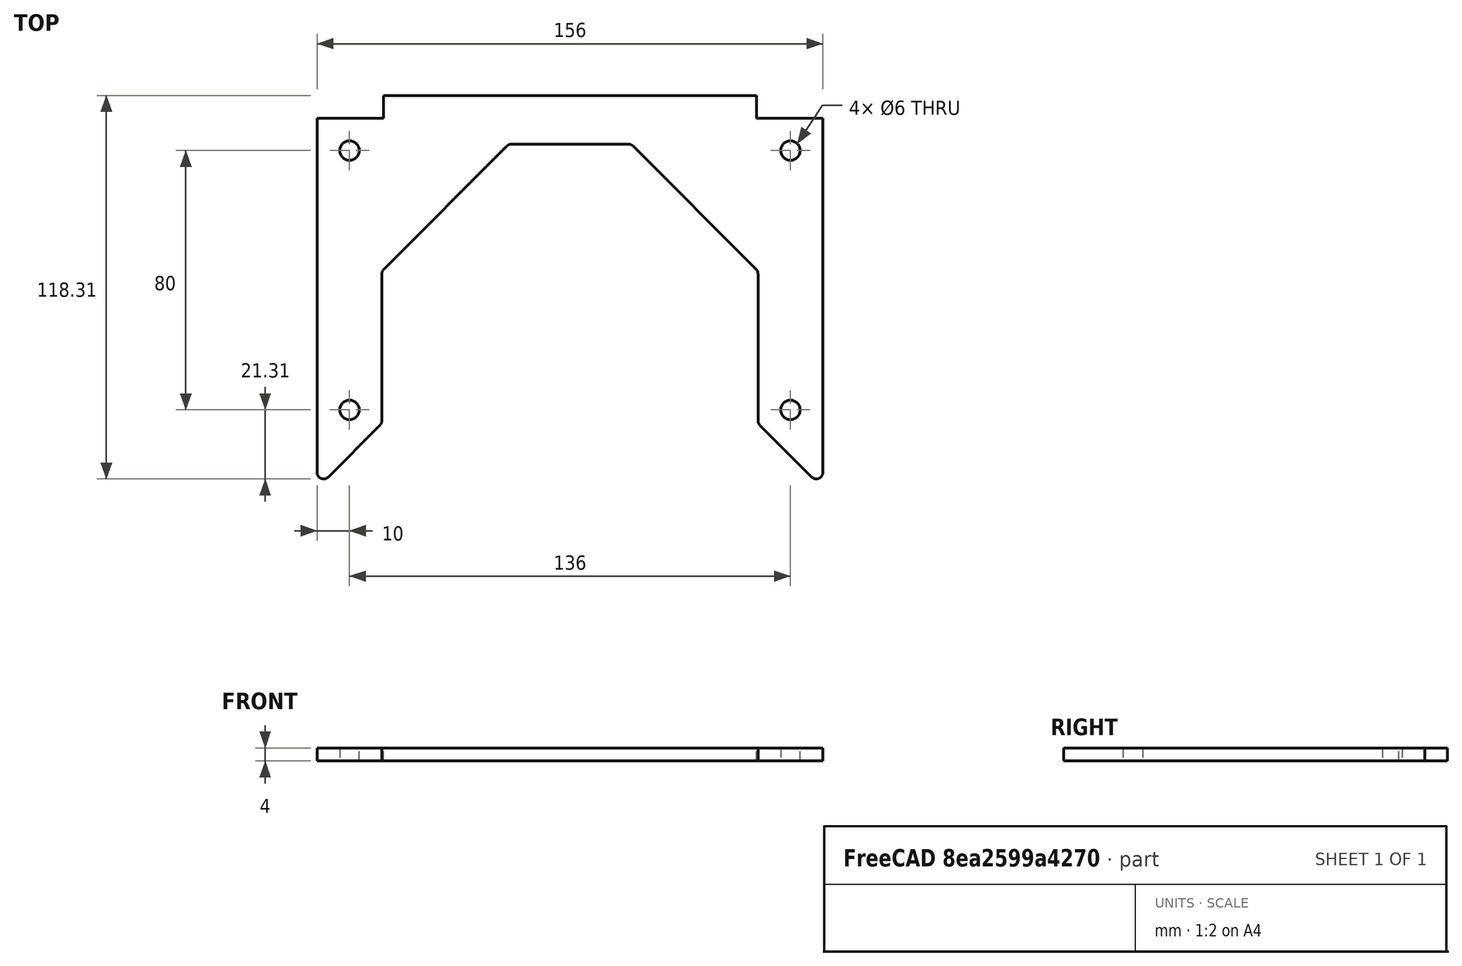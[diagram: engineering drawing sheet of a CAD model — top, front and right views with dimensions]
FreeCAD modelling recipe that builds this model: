
FCSTD DOCUMENT  (FreeCAD 0.19R24267 +99 (Git))
Label: V2 Enclosure middle U bracket slotted panel without cable notch
License: All rights reserved
LicenseURL: http://en.wikipedia.org/wiki/All_rights_reserved
objects: Sketcher::SketchObject×1, PartDesign::Pad×1, PartDesign::Body×1
note: 4 computed .brp shape members not serialized (recipe doc carries the construction recipe); baked Part::Feature solids carry a one-line shape summary decoded from their .brp

FEATURE [Sketcher::SketchObject] Sketch
  FullyConstrained = true
  MapMode = 5
  Support = -> [XY_Plane]
  sketch-geometry (35):
    g0: LineSegment StartX=-68 StartY=0 StartZ=0 EndX=-68 EndY=-114.142 EndZ=0
    g1: Circle CenterX=-68 CenterY=-100 CenterZ=0 NormalX=0 NormalY=0 NormalZ=1 AngleXU=0 Radius=3
    g2: LineSegment StartX=68 StartY=0 StartZ=0 EndX=68 EndY=-114.142 EndZ=0
    g3: Circle CenterX=68 CenterY=-100 CenterZ=0 NormalX=0 NormalY=0 NormalZ=1 AngleXU=0 Radius=3
    g4: LineSegment StartX=-78 StartY=-10 StartZ=0 EndX=-78 EndY=-119.314 EndZ=0
    g5: LineSegment StartX=-58 StartY=-58 StartZ=0 EndX=-58 EndY=-103.314 EndZ=0
    g6: LineSegment StartX=-57.4142 StartY=-56.5858 StartZ=0 EndX=-19.4142 EndY=-18.5858 EndZ=0
    g7: LineSegment StartX=19.4142 StartY=-18.5858 StartZ=0 EndX=57.4142 EndY=-56.5858 EndZ=0
    g8: LineSegment StartX=58 StartY=-58 StartZ=0 EndX=58 EndY=-103.314 EndZ=0
    g9: LineSegment StartX=58.5858 StartY=-104.728 StartZ=0 EndX=74.5858 EndY=-120.728 EndZ=0
    g10: LineSegment StartX=78 StartY=-119.314 StartZ=0 EndX=78 EndY=-10 EndZ=0
    g11: LineSegment StartX=57.5 StartY=10 StartZ=0 EndX=-57.5 EndY=10 EndZ=0
    g12: LineSegment StartX=-74.5858 StartY=-120.728 StartZ=0 EndX=-58.5858 EndY=-104.728 EndZ=0
    g13: ArcOfCircle CenterX=-76 CenterY=-119.314 CenterZ=0 NormalX=0 NormalY=0 NormalZ=1 AngleXU=0 Radius=2 StartAngle=3.14159 EndAngle=5.49779
    g14: ArcOfCircle CenterX=-60 CenterY=-103.314 CenterZ=0 NormalX=0 NormalY=0 NormalZ=1 AngleXU=0 Radius=2 StartAngle=5.49779 EndAngle=6.28319
    g15: ArcOfCircle CenterX=60 CenterY=-103.314 CenterZ=0 NormalX=0 NormalY=0 NormalZ=1 AngleXU=0 Radius=2 StartAngle=3.14159 EndAngle=3.92699
    g16: ArcOfCircle CenterX=76 CenterY=-119.314 CenterZ=0 NormalX=0 NormalY=0 NormalZ=1 AngleXU=0 Radius=2 StartAngle=3.92699 EndAngle=6.28319
    g17: ArcOfCircle CenterX=-56 CenterY=-58 CenterZ=0 NormalX=0 NormalY=0 NormalZ=1 AngleXU=0 Radius=2 StartAngle=2.35619 EndAngle=3.14159
    g18: ArcOfCircle CenterX=-18 CenterY=-20 CenterZ=0 NormalX=0 NormalY=0 NormalZ=1 AngleXU=0 Radius=2 StartAngle=1.5708 EndAngle=2.35619
    g19: ArcOfCircle CenterX=18 CenterY=-20 CenterZ=0 NormalX=0 NormalY=0 NormalZ=1 AngleXU=0 Radius=2 StartAngle=0.785398 EndAngle=1.5708
    g20: ArcOfCircle CenterX=56 CenterY=-58 CenterZ=0 NormalX=0 NormalY=0 NormalZ=1 AngleXU=0 Radius=2 StartAngle=0 EndAngle=0.785398
    g21: Circle CenterX=-68 CenterY=-100 CenterZ=0 NormalX=0 NormalY=0 NormalZ=1 AngleXU=0 Radius=10
    g22: Circle CenterX=68 CenterY=-100 CenterZ=0 NormalX=0 NormalY=0 NormalZ=1 AngleXU=0 Radius=10
    g23: GeomPoint X=0 Y=-10 Z=0
    g24: GeomPoint X=0 Y=10 Z=0
    g25: LineSegment StartX=-78 StartY=-10 StartZ=0 EndX=-57.5 EndY=-10 EndZ=0
    g26: LineSegment StartX=57.5 StartY=-10 StartZ=0 EndX=78 EndY=-10 EndZ=0
    g27: LineSegment StartX=-57.5 StartY=-10 StartZ=0 EndX=-57.5 EndY=-3 EndZ=0
    g28: LineSegment StartX=-57.5 StartY=-3 StartZ=0 EndX=-57.5 EndY=10 EndZ=0
    g29: LineSegment StartX=57.5 StartY=10 StartZ=0 EndX=57.5 EndY=-3 EndZ=0
    g30: LineSegment StartX=57.5 StartY=-3 StartZ=0 EndX=57.5 EndY=-10 EndZ=0
    g31: LineSegment StartX=57.5 StartY=-3 StartZ=0 EndX=-57.5 EndY=-3 EndZ=0
    g32: LineSegment StartX=-18 StartY=-18 StartZ=0 EndX=18 EndY=-18 EndZ=0
    g33: Circle CenterX=-68 CenterY=-20 CenterZ=0 NormalX=0 NormalY=0 NormalZ=1 AngleXU=0 Radius=3
    g34: Circle CenterX=68 CenterY=-20 CenterZ=0 NormalX=0 NormalY=0 NormalZ=1 AngleXU=0 Radius=3
  constraints (85):
    c: Vertical(g0)
    c: PointOnObject(g1,g0)
    c: Vertical(g2)
    c: Symmetric(g1,g3,g-2)
    c: Vertical(g4)
    c: Vertical(g5)
    c: Vertical(g10)
    c: Horizontal(g11)
    c: Tangent(g4,g13) = -1.5708
    c: Tangent(g12,g13) = -1.5708
    c: Tangent(g5,g14) = 1.5708
    c: Tangent(g12,g14) = -1.5708
    c: Tangent(g8,g15) = -1.5708
    c: Tangent(g9,g15) = -1.5708
    c: Tangent(g10,g16) = -1.5708
    c: Tangent(g9,g16) = -1.5708
    c: Tangent(g6,g17) = 1.5708
    c: Tangent(g5,g17) = -1.5708
    c: Tangent(g6,g18) = 1.5708
    c: Tangent(g7,g19) = 1.5708
    c: Tangent(g7,g20) = 1.5708
    c: Tangent(g8,g20) = 1.5708
    c: Equal(g17,g18)
    c: Equal(g19,g20)
    c: Equal(g20,g16)
    c: Equal(g16,g15)
    c: Equal(g15,g13)
    c: Equal(g13,g14)
    c: PointOnObject(g0,g12)
    c: PointOnObject(g2,g9)
    c: Coincident(g21,g1)
    c: Coincident(g22,g3)
    c: Tangent(g22,g10)
    c: Tangent(g22,g9)
    c: Tangent(g8,g22)
    c: Tangent(g4,g21)
    c: Angle(g12,g4) = 0.785398
    c: Symmetric(g5,g8,g-2)
    c: DistanceX(g4,g5) = 20
    c: Symmetric(g4,g10,g-2)
    c: Symmetric(g5,g8,g-2)
    c: PointOnObject(g23,g-2)
    c: PointOnObject(g24,g11)
    c: Symmetric(g24,g23,g-1)
    c: DistanceY(g23,g24) = 20
    c: DistanceX(g0,g2) = 136
    c: DistanceY(g1,g0) = 100
    c: PointOnObject(g0,g-1)
    c: Horizontal(g25)
    c: Horizontal(g26)
    c: Coincident(g4,g25)
    c: Coincident(g10,g26)
    c: Equal(g18,g13)
    c: Radius(g18) = 2
    c: DistanceX(g25,g25) = 20.5
    c: Symmetric(g0,g2,g-1)
    c: Coincident(g27,g25)
    c: Coincident(g28,g27)
    c: Coincident(g28,g11)
    c: Vertical(g28)
    c: Coincident(g29,g11)
    c: Vertical(g29)
    c: Coincident(g30,g29)
    c: Coincident(g30,g26)
    c: Vertical(g30)
    c: Coincident(g31,g29)
    c: Coincident(g31,g27)
    c: Horizontal(g31)
    c: Vertical(g27)
    c: Symmetric(g25,g26,g-2)
    c: DistanceY(g4,g11) = 20
    c: DistanceY(g30,g30) = 7
    c: Tangent(g19,g32) = 1.5708
    c: Tangent(g18,g32) = 1.5708
    c: Symmetric(g18,g19,g-2)
    c: DistanceY(g19,g30) = 15
    c: DistanceY(g5,g18) = 40
    c: DistanceX(g5,g18) = 40
    c: Radius(g1) = 3
    c: Equal(g3,g1)
    c: PointOnObject(g33,g0)
    c: Symmetric(g34,g33,g-2)
    c: Equal(g33,g1)
    c: Equal(g1,g34)
    c: DistanceY(g33,g0) = 20
FEATURE [PartDesign::Pad] Pad
  Direction = (1,1,1)
  Length = 4
  Length2 = 100
  Profile = -> Sketch
  Type = 0
FEATURE [PartDesign::Body] Body
  Group = -> [Sketch,Pad]
  Origin = -> Origin
  Tip = -> Pad
